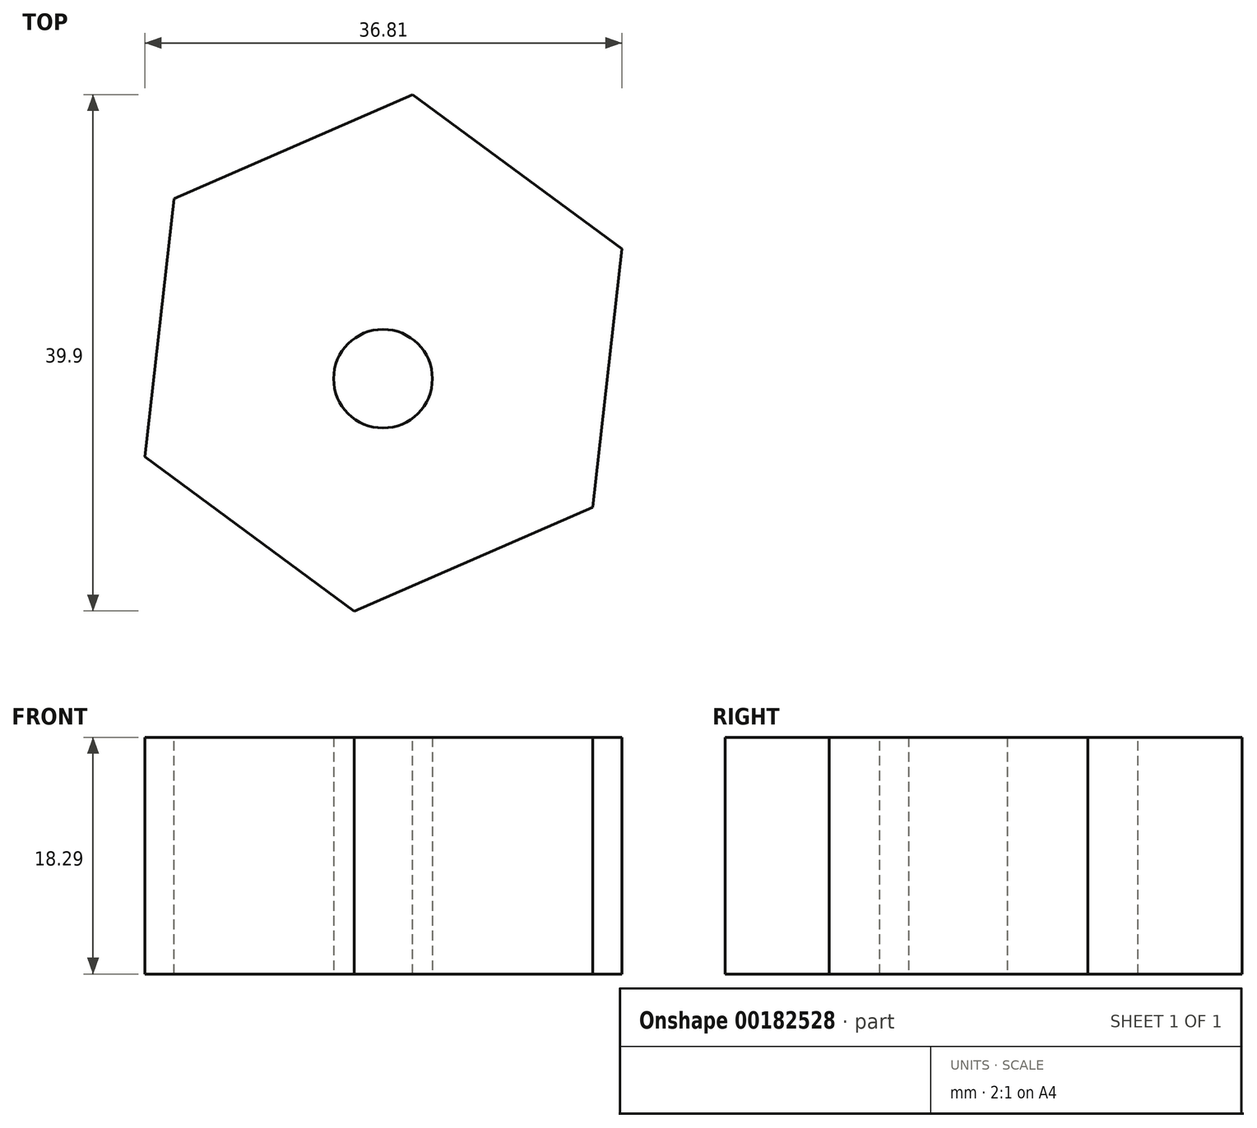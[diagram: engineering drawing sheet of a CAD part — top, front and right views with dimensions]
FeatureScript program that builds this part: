
annotation { "Feature Type Name" : "Feature", "Feature Type Description" : "" }
export const myFeature = defineFeature(function(context is Context, id is Id, definition is map)
    precondition{}
    {
        {
            var Q0;
            Q0=qCreatedBy(makeId("Top.planeOp"),FACE);
            var sketch = newSketch(context, id + "F0", { "sketchPlane" : qUnion([Q0])});
            skCircle(sketch, "E0.cCircle", {"center": v(2.08, 9.35) * mm, "radius": 17.39 * mm, "construction": true});
            skLineSegment(sketch, "E0.0", {"start": v(-0.17, -10.6) * mm, "end": v(-16.33, 1.32) * mm});
            skLineSegment(sketch, "E0.1", {"start": v(-16.33, 1.32) * mm, "end": v(-14.08, 21.27) * mm});
            skLineSegment(sketch, "E0.2", {"start": v(-14.08, 21.27) * mm, "end": v(4.32, 29.3) * mm});
            skLineSegment(sketch, "E0.3", {"start": v(4.32, 29.3) * mm, "end": v(20.48, 17.38) * mm});
            skLineSegment(sketch, "E0.4", {"start": v(20.48, 17.38) * mm, "end": v(18.23, -2.57) * mm});
            skLineSegment(sketch, "E0.5", {"start": v(18.23, -2.57) * mm, "end": v(-0.17, -10.6) * mm});
            skPoint(sketch, "E0.0.midPoint", {"position": v(-8.25, -4.64) * mm});
            skSolve(sketch);
        }
        {
            var Q0;
            Q0 = qSketchRegion(id + "F0", true);
            extrude(context, id + "F1", {"entities" : qUnion([Q0]), "oppositeDirection" : true, "depth" : 18.29 * mm});
        }
        {
            var Q0;
            Q0=makeQuery(id+"F1.opExtrude","CAP_FACE",FACE,{"disambiguationData":[OSD([sQuery(id+"F0.wireOp",EDGE,"E0.0"),sQuery(id+"F0.wireOp",EDGE,"E0.1"),sQuery(id+"F0.wireOp",EDGE,"E0.2"),sQuery(id+"F0.wireOp",EDGE,"E0.3"),sQuery(id+"F0.wireOp",EDGE,"E0.4"),sQuery(id+"F0.wireOp",EDGE,"E0.5")])],"isStart":false});
            var sketch = newSketch(context, id + "F2", { "sketchPlane" : qUnion([Q0])});
            skCircle(sketch, "E1", {"center": v(2.05, -7.35) * mm, "radius": 3.14 * mm});
            skSolve(sketch);
        }
        {
            var Q0;
            Q0=sQuery(id+"F2.wireOp",VERTEX,"E1.center");
            var Q1;
            Q1=makeQuery(id+"F1.opExtrude","SWEPT_BODY",BODY,{"disambiguationData":[OSD([sQuery(id+"F0.wireOp",EDGE,"E0.0"),sQuery(id+"F0.wireOp",EDGE,"E0.1"),sQuery(id+"F0.wireOp",EDGE,"E0.2"),sQuery(id+"F0.wireOp",EDGE,"E0.3"),sQuery(id+"F0.wireOp",EDGE,"E0.4"),sQuery(id+"F0.wireOp",EDGE,"E0.5")])]});
            hole(context, id + "F3", {"style" : HoleStyle.SIMPLE, "endStyle" : HoleEndStyle.THROUGH, "holeDiameter" : 7.62 * mm, "startFromSketch" : true, "locations" : qUnion([Q0]), "scope" : qUnion([Q1]), "isTappedThrough" : true});
        }
    });
